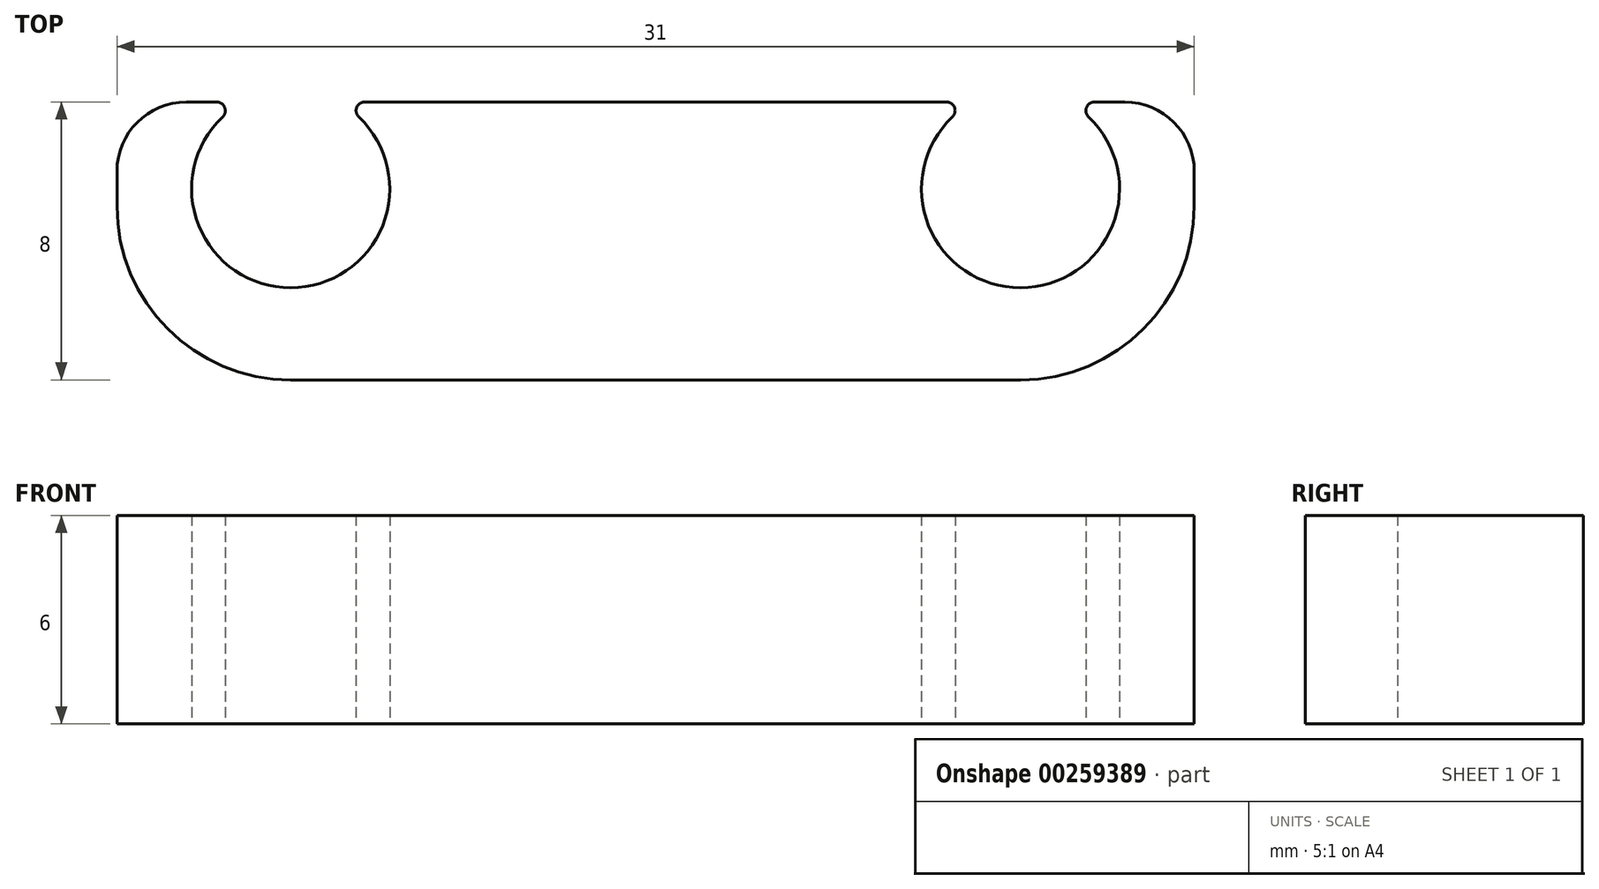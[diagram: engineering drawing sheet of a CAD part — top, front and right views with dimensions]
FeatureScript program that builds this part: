
annotation { "Feature Type Name" : "Feature", "Feature Type Description" : "" }
export const myFeature = defineFeature(function(context is Context, id is Id, definition is map)
    precondition{}
    {
        {
            var Q0;
            Q0=qCreatedBy(makeId("Top.planeOp"),FACE);
            var sketch = newSketch(context, id + "F0", { "sketchPlane" : qUnion([Q0])});
            skLineSegment(sketch, "E0.bottom", {"start": v(-15.5, 4) * mm, "end": v(15.5, 4) * mm});
            skLineSegment(sketch, "E0.top", {"start": v(-15.5, -4) * mm, "end": v(15.5, -4) * mm});
            skLineSegment(sketch, "E0.left", {"start": v(-15.5, 4) * mm, "end": v(-15.5, -4) * mm});
            skLineSegment(sketch, "E0.right", {"start": v(15.5, 4) * mm, "end": v(15.5, -4) * mm});
            skPoint(sketch, "E0.middle", {"position": v(0, 0) * mm});
            skLineSegment(sketch, "E1", {"start": v(-15.5, 1.5) * mm, "end": v(15.5, 1.5) * mm, "construction": true});
            skCircle(sketch, "E2", {"center": v(-10.5, 1.5) * mm, "radius": 2.85 * mm});
            skCircle(sketch, "E3", {"center": v(10.5, 1.5) * mm, "radius": 2.85 * mm});
            skSolve(sketch);
        }
        {
            var Q0;
            Q0=makeQuery(id+"F0.imprint","IMPRINT",FACE,{"disambiguationData":[TD([[makeQuery(id+"F0.imprint","IMPRINT",EDGE,{"derivedFrom":sQuery(id+"F0.wireOp",EDGE,"E0.top")}),1.0]])]});
            extrude(context, id + "F1", {"entities" : qUnion([Q0]), "depth" : 6 * mm});
        }
        {
            var Q0;
            Q0=makeQuery(id+"F1.opExtrude","SWEPT_EDGE",EDGE,{"disambiguationData":[OSD([sQuery(id+"F0.wireOp",EDGE,"E0.top"),sQuery(id+"F0.wireOp",EDGE,"E0.right")])]});
            var Q1;
            Q1=makeQuery(id+"F1.opExtrude","SWEPT_EDGE",EDGE,{"disambiguationData":[OSD([sQuery(id+"F0.wireOp",EDGE,"E0.top"),sQuery(id+"F0.wireOp",EDGE,"E0.left")])]});
            fillet(context, id + "F2", {"entities" : qUnion([Q0, Q1]), "radius" : 5 * mm, "tangentPropagation" : true, "allowEdgeOverflow" : false});
        }
        {
            var Q0;
            {var subQ0=sQuery(id+"F0.wireOp",EDGE,"E0.right");var subQ1=sQuery(id+"F0.wireOp",EDGE,"E0.bottom");Q0=makeQuery(id+"F2.opFillet","BLEND_EDGE",EDGE,{"blendedFrom":[makeQuery(id+"F1.opExtrude","SWEPT_EDGE",EDGE,{"disambiguationData":[OSD([sQuery(id+"F0.wireOp",EDGE,"E0.top"),subQ0])]}),makeQuery(id+"F1.opExtrude","SWEPT_FACE",FACE,{"disambiguationData":[OSD([subQ1]),TDD([makeQuery(id+"F0.imprint","IMPRINT",EDGE,{"disambiguationData":[TD([[makeQuery(id+"F0.imprint","INTERSECT",VERTEX,{"derivedFrom":[subQ1,subQ0]}),1.0]])],"derivedFrom":subQ1})])]})],"blendedInto":[makeQuery(id+"F1.opExtrude","SWEPT_FACE",FACE,{"disambiguationData":[OSD([subQ1]),TDD([makeQuery(id+"F0.imprint","IMPRINT",EDGE,{"disambiguationData":[TD([[makeQuery(id+"F0.imprint","INTERSECT",VERTEX,{"derivedFrom":[subQ1,subQ0]}),1.0]])],"derivedFrom":subQ1})])]})]});}
            var Q1;
            {var subQ0=sQuery(id+"F0.wireOp",EDGE,"E0.left");var subQ1=sQuery(id+"F0.wireOp",EDGE,"E0.bottom");Q1=makeQuery(id+"F2.opFillet","BLEND_EDGE",EDGE,{"blendedFrom":[makeQuery(id+"F1.opExtrude","SWEPT_EDGE",EDGE,{"disambiguationData":[OSD([sQuery(id+"F0.wireOp",EDGE,"E0.top"),subQ0])]}),makeQuery(id+"F1.opExtrude","SWEPT_FACE",FACE,{"disambiguationData":[OSD([subQ1]),TDD([makeQuery(id+"F0.imprint","IMPRINT",EDGE,{"disambiguationData":[TD([[makeQuery(id+"F0.imprint","INTERSECT",VERTEX,{"derivedFrom":[subQ1,subQ0]}),-1.0]])],"derivedFrom":subQ1})])]})],"blendedInto":[makeQuery(id+"F1.opExtrude","SWEPT_FACE",FACE,{"disambiguationData":[OSD([subQ1]),TDD([makeQuery(id+"F0.imprint","IMPRINT",EDGE,{"disambiguationData":[TD([[makeQuery(id+"F0.imprint","INTERSECT",VERTEX,{"derivedFrom":[subQ1,subQ0]}),-1.0]])],"derivedFrom":subQ1})])]})]});}
            var Q2;
            Q2=makeQuery(id+"F1.opExtrude","SWEPT_EDGE",EDGE,{"disambiguationData":[OSD([sQuery(id+"F0.wireOp",EDGE,"E0.bottom"),sQuery(id+"F0.wireOp",EDGE,"E0.left")])]});
            var Q3;
            Q3=makeQuery(id+"F1.opExtrude","SWEPT_EDGE",EDGE,{"disambiguationData":[OSD([sQuery(id+"F0.wireOp",EDGE,"E0.bottom"),sQuery(id+"F0.wireOp",EDGE,"E0.right")])]});
            fillet(context, id + "F3", {"entities" : qUnion([Q0, Q1, Q2, Q3]), "radius" : 2 * mm, "tangentPropagation" : true, "allowEdgeOverflow" : false});
        }
        {
            var Q0;
            {var subQ0=sQuery(id+"F0.wireOp",EDGE,"E3");var subQ1=sQuery(id+"F0.wireOp",EDGE,"E0.bottom");Q0=makeQuery(id+"F1.opExtrude","SWEPT_EDGE",EDGE,{"disambiguationData":[OSD([subQ1,subQ0]),TDD([makeQuery(id+"F0.imprint","INTERSECT",VERTEX,{"disambiguationData":[OD(0.0)],"derivedFrom":[subQ1,subQ0]})])]});}
            var Q1;
            {var subQ0=sQuery(id+"F0.wireOp",EDGE,"E3");var subQ1=sQuery(id+"F0.wireOp",EDGE,"E0.bottom");Q1=makeQuery(id+"F1.opExtrude","SWEPT_EDGE",EDGE,{"disambiguationData":[OSD([subQ1,subQ0]),TDD([makeQuery(id+"F0.imprint","INTERSECT",VERTEX,{"disambiguationData":[OD(1.0)],"derivedFrom":[subQ1,subQ0]})])]});}
            var Q2;
            {var subQ0=sQuery(id+"F0.wireOp",EDGE,"E2");var subQ1=sQuery(id+"F0.wireOp",EDGE,"E0.bottom");Q2=makeQuery(id+"F1.opExtrude","SWEPT_EDGE",EDGE,{"disambiguationData":[OSD([subQ1,subQ0]),TDD([makeQuery(id+"F0.imprint","INTERSECT",VERTEX,{"disambiguationData":[OD(1.0)],"derivedFrom":[subQ1,subQ0]})])]});}
            var Q3;
            {var subQ0=sQuery(id+"F0.wireOp",EDGE,"E2");var subQ1=sQuery(id+"F0.wireOp",EDGE,"E0.bottom");Q3=makeQuery(id+"F1.opExtrude","SWEPT_EDGE",EDGE,{"disambiguationData":[OSD([subQ1,subQ0]),TDD([makeQuery(id+"F0.imprint","INTERSECT",VERTEX,{"disambiguationData":[OD(0.0)],"derivedFrom":[subQ1,subQ0]})])]});}
            fillet(context, id + "F4", {"entities" : qUnion([Q0, Q1, Q2, Q3]), "radius" : 0.25 * mm, "tangentPropagation" : true, "allowEdgeOverflow" : false});
        }
    });
